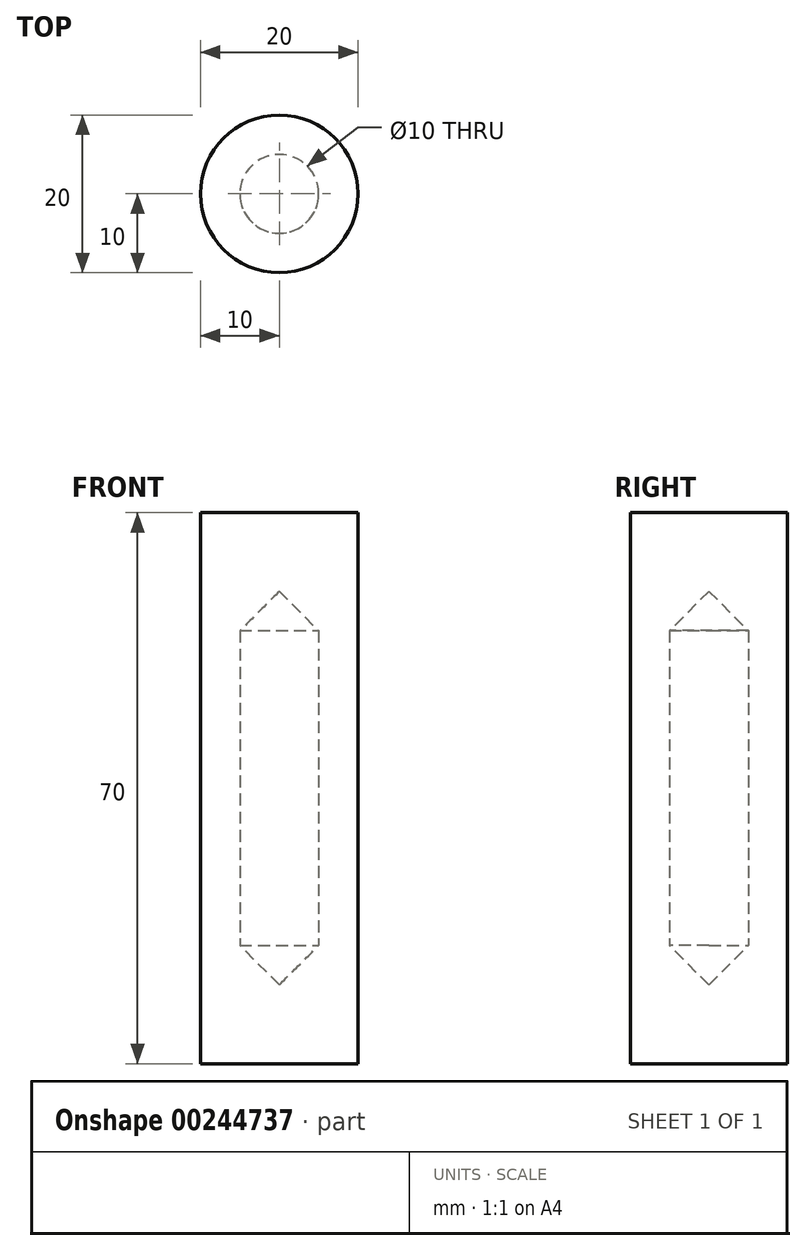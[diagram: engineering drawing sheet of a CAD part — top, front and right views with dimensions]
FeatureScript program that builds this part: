
annotation { "Feature Type Name" : "Feature", "Feature Type Description" : "" }
export const myFeature = defineFeature(function(context is Context, id is Id, definition is map)
    precondition{}
    {
        {
            var Q0;
            Q0=qCreatedBy(makeId("Front.planeOp"),FACE);
            var sketch = newSketch(context, id + "F0", { "sketchPlane" : qUnion([Q0])});
            skLineSegment(sketch, "E0", {"start": v(0, 0) * mm, "end": v(10, 0) * mm});
            skLineSegment(sketch, "E1", {"start": v(10, 0) * mm, "end": v(10, 70) * mm});
            skLineSegment(sketch, "E2", {"start": v(10, 70) * mm, "end": v(0, 70) * mm});
            skLineSegment(sketch, "E3", {"start": v(0, 0) * mm, "end": v(0, 10) * mm});
            skLineSegment(sketch, "E4", {"start": v(0, 60) * mm, "end": v(0, 70) * mm});
            skLineSegment(sketch, "E5", {"start": v(0, 10) * mm, "end": v(5, 15) * mm});
            skLineSegment(sketch, "E6", {"start": v(5, 15) * mm, "end": v(5, 55) * mm});
            skLineSegment(sketch, "E7", {"start": v(0, 60) * mm, "end": v(5, 55) * mm});
            skSolve(sketch);
        }
        {
            var Q0;
            Q0 = qSketchRegion(id + "F0", true);
            var Q1;
            Q1=sQuery(id+"F0.wireOp",EDGE,"E3");
            revolve(context, id + "F1", {"entities" : qUnion([Q0]), "axis" : qUnion([Q1]), "revolveType" : RevolveType.FULL});
        }
    });
